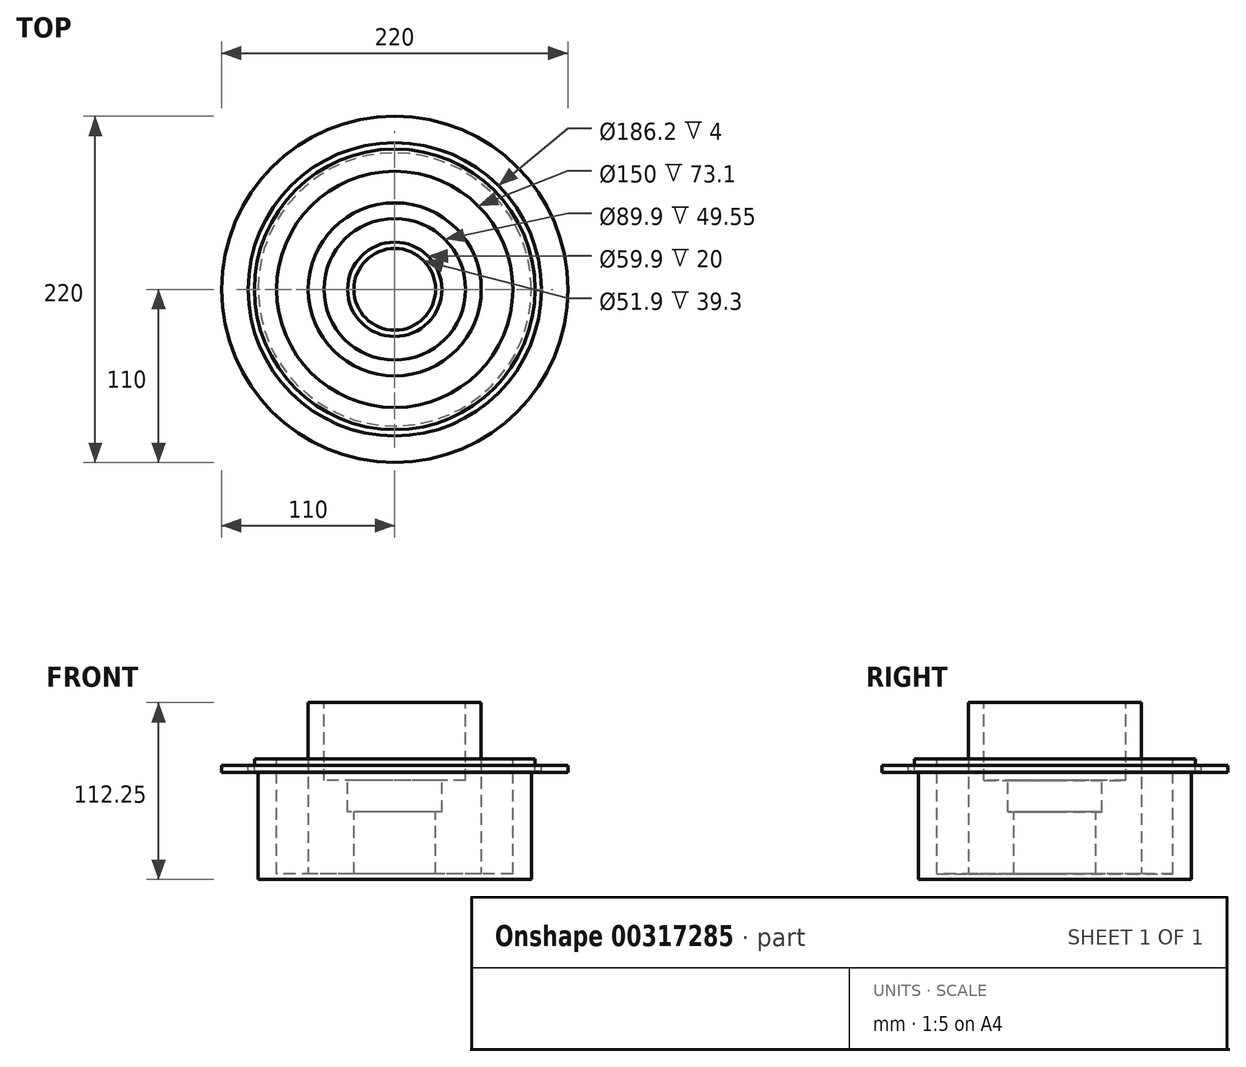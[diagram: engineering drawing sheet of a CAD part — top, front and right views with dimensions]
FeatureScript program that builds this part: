
annotation { "Feature Type Name" : "Feature", "Feature Type Description" : "" }
export const myFeature = defineFeature(function(context is Context, id is Id, definition is map)
    precondition{}
    {
        {
            var Q0;
            Q0=qCreatedBy(makeId("Top.planeOp"),FACE);
            var sketch = newSketch(context, id + "F0", { "sketchPlane" : qUnion([Q0])});
            skCircle(sketch, "E0", {"center": v(0, 0) * mm, "radius": 86.75 * mm});
            skSolve(sketch);
        }
        {
            var Q0;
            Q0=makeQuery(id+"F0.imprint","IMPRINT",FACE,{"disambiguationData":[TD([[makeQuery(id+"F0.imprint","IMPRINT",EDGE,{"derivedFrom":sQuery(id+"F0.wireOp",EDGE,"E0")}),1.0]])]});
            extrude(context, id + "F1", {"entities" : qUnion([Q0]), "depth" : 76.5 * mm});
        }
        {
            var Q0;
            Q0=makeQuery(id+"F1.opExtrude","CAP_FACE",FACE,{"disambiguationData":[OSD([sQuery(id+"F0.wireOp",EDGE,"E0")])],"isStart":false});
            var sketch = newSketch(context, id + "F2", { "sketchPlane" : qUnion([Q0])});
            skCircle(sketch, "E1", {"center": v(0, 0) * mm, "radius": 110 * mm});
            skSolve(sketch);
        }
        {
            var Q0;
            Q0 = qSketchRegion(id + "F2", true);
            extrude(context, id + "F3", {"entities" : qUnion([Q0]), "operationType" : NewBodyOperationType.ADD, "oppositeDirection" : true, "depth" : 8.7 * mm});
        }
        {
            var Q0;
            Q0=makeQuery(id+"F3.boolean.opBoolean","MERGE",FACE,{"derivedFrom":[makeQuery(id+"F1.opExtrude","CAP_FACE",FACE,{"disambiguationData":[OSD([sQuery(id+"F0.wireOp",EDGE,"E0")])],"isStart":false}),makeQuery(id+"F3.opExtrude","CAP_FACE",FACE,{"disambiguationData":[OSD([sQuery(id+"F2.wireOp",EDGE,"E1")])],"isStart":true})]});
            var sketch = newSketch(context, id + "F4", { "sketchPlane" : qUnion([Q0])});
            skCircle(sketch, "E2", {"center": v(0, 0) * mm, "radius": 93.1 * mm});
            skCircle(sketch, "E3", {"center": v(0, 0) * mm, "radius": 89.1 * mm});
            skCircle(sketch, "E4", {"center": v(0, 0) * mm, "radius": 75 * mm});
            skSolve(sketch);
        }
        {
            var Q0;
            Q0=makeQuery(id+"F4.imprint","IMPRINT",FACE,{"disambiguationData":[TD([[makeQuery(id+"F4.imprint","IMPRINT",EDGE,{"derivedFrom":sQuery(id+"F4.wireOp",EDGE,"E2")}),-1.0]])]});
            var Q1;
            Q1=makeQuery(id+"F4.imprint","IMPRINT",FACE,{"disambiguationData":[TD([[makeQuery(id+"F4.imprint","IMPRINT",EDGE,{"derivedFrom":sQuery(id+"F4.wireOp",EDGE,"E2")}),1.0]])]});
            extrude(context, id + "F5", {"entities" : qUnion([Q0, Q1]), "operationType" : NewBodyOperationType.REMOVE, "oppositeDirection" : true, "depth" : 4 * mm});
        }
        {
            var Q0;
            Q0=makeQuery(id+"F5.boolean.opBoolean","COPY",FACE,{"derivedFrom":makeQuery(id+"F5.opExtrude","CAP_FACE",FACE,{"disambiguationData":[OSD([sQuery(id+"F2.wireOp",EDGE,"E1"),sQuery(id+"F4.wireOp",EDGE,"E3")])],"isStart":false})});
            var sketch = newSketch(context, id + "F6", { "sketchPlane" : qUnion([Q0])});
            skCircle(sketch, "E5", {"center": v(0, 0) * mm, "radius": 93.1 * mm});
            skSolve(sketch);
        }
        {
            var Q0;
            Q0=makeQuery(id+"F6.imprint","IMPRINT",FACE,{"disambiguationData":[TD([[makeQuery(id+"F6.imprint","IMPRINT",EDGE,{"derivedFrom":sQuery(id+"F6.wireOp",EDGE,"E5")}),1.0]])]});
            extrude(context, id + "F7", {"entities" : qUnion([Q0]), "operationType" : NewBodyOperationType.REMOVE, "oppositeDirection" : true, "depth" : 4 * mm});
        }
        {
            var Q0;
            Q0=makeQuery(id+"F3.boolean.opBoolean","MERGE",FACE,{"derivedFrom":[makeQuery(id+"F1.opExtrude","CAP_FACE",FACE,{"disambiguationData":[OSD([sQuery(id+"F0.wireOp",EDGE,"E0")])],"isStart":false}),makeQuery(id+"F3.opExtrude","CAP_FACE",FACE,{"disambiguationData":[OSD([sQuery(id+"F2.wireOp",EDGE,"E1")])],"isStart":true})]});
            var sketch = newSketch(context, id + "F8", { "sketchPlane" : qUnion([Q0])});
            skCircle(sketch, "E6", {"center": v(0, 0) * mm, "radius": 75 * mm});
            skSolve(sketch);
        }
        {
            var Q0;
            Q0 = qSketchRegion(id + "F8", true);
            extrude(context, id + "F9", {"entities" : qUnion([Q0]), "operationType" : NewBodyOperationType.REMOVE, "oppositeDirection" : true, "depth" : 73.1 * mm});
        }
        {
            var Q0;
            Q0=makeQuery(id+"F9.boolean.opBoolean","COPY",FACE,{"derivedFrom":makeQuery(id+"F9.opExtrude","CAP_FACE",FACE,{"disambiguationData":[OSD([sQuery(id+"F8.wireOp",EDGE,"E6")])],"isStart":false})});
            var sketch = newSketch(context, id + "F10", { "sketchPlane" : qUnion([Q0])});
            skCircle(sketch, "E7", {"center": v(0, 0) * mm, "radius": 54.95 * mm});
            skSolve(sketch);
        }
        {
            var Q0;
            Q0=makeQuery(id+"F10.imprint","IMPRINT",FACE,{"disambiguationData":[TD([[makeQuery(id+"F10.imprint","IMPRINT",EDGE,{"derivedFrom":sQuery(id+"F10.wireOp",EDGE,"E7")}),1.0]])]});
            extrude(context, id + "F11", {"entities" : qUnion([Q0]), "operationType" : NewBodyOperationType.ADD, "depth" : 108.85 * mm});
        }
        {
            var Q0;
            Q0=makeQuery(id+"F11.opExtrude","CAP_FACE",FACE,{"disambiguationData":[OSD([sQuery(id+"F10.wireOp",EDGE,"E7")])],"isStart":false});
            var sketch = newSketch(context, id + "F12", { "sketchPlane" : qUnion([Q0])});
            skCircle(sketch, "E8", {"center": v(0, 0) * mm, "radius": 44.95 * mm});
            skSolve(sketch);
        }
        {
            var Q0;
            Q0 = qSketchRegion(id + "F12", true);
            extrude(context, id + "F13", {"entities" : qUnion([Q0]), "operationType" : NewBodyOperationType.REMOVE, "oppositeDirection" : true, "depth" : 49.55 * mm});
        }
        {
            var Q0;
            Q0=makeQuery(id+"F13.boolean.opBoolean","COPY",FACE,{"derivedFrom":makeQuery(id+"F13.opExtrude","CAP_FACE",FACE,{"disambiguationData":[OSD([sQuery(id+"F12.wireOp",EDGE,"E8")])],"isStart":false})});
            var sketch = newSketch(context, id + "F14", { "sketchPlane" : qUnion([Q0])});
            skCircle(sketch, "E9", {"center": v(0, 0) * mm, "radius": 29.95 * mm});
            skSolve(sketch);
        }
        {
            var Q0;
            Q0=makeQuery(id+"F14.imprint","IMPRINT",FACE,{"disambiguationData":[TD([[makeQuery(id+"F14.imprint","IMPRINT",EDGE,{"derivedFrom":sQuery(id+"F14.wireOp",EDGE,"E9")}),1.0]])]});
            extrude(context, id + "F15", {"entities" : qUnion([Q0]), "operationType" : NewBodyOperationType.REMOVE, "oppositeDirection" : true, "depth" : 20 * mm});
        }
        {
            var Q0;
            Q0=makeQuery(id+"F15.boolean.opBoolean","COPY",FACE,{"derivedFrom":makeQuery(id+"F15.opExtrude","CAP_FACE",FACE,{"disambiguationData":[OSD([sQuery(id+"F14.wireOp",EDGE,"E9")])],"isStart":false})});
            var sketch = newSketch(context, id + "F16", { "sketchPlane" : qUnion([Q0])});
            skCircle(sketch, "E10", {"center": v(0, 0) * mm, "radius": 25.95 * mm});
            skSolve(sketch);
        }
        {
            var Q0;
            Q0 = qSketchRegion(id + "F16", true);
            extrude(context, id + "F17", {"entities" : qUnion([Q0]), "operationType" : NewBodyOperationType.REMOVE, "oppositeDirection" : true, "depth" : 39.3 * mm});
        }
    });
